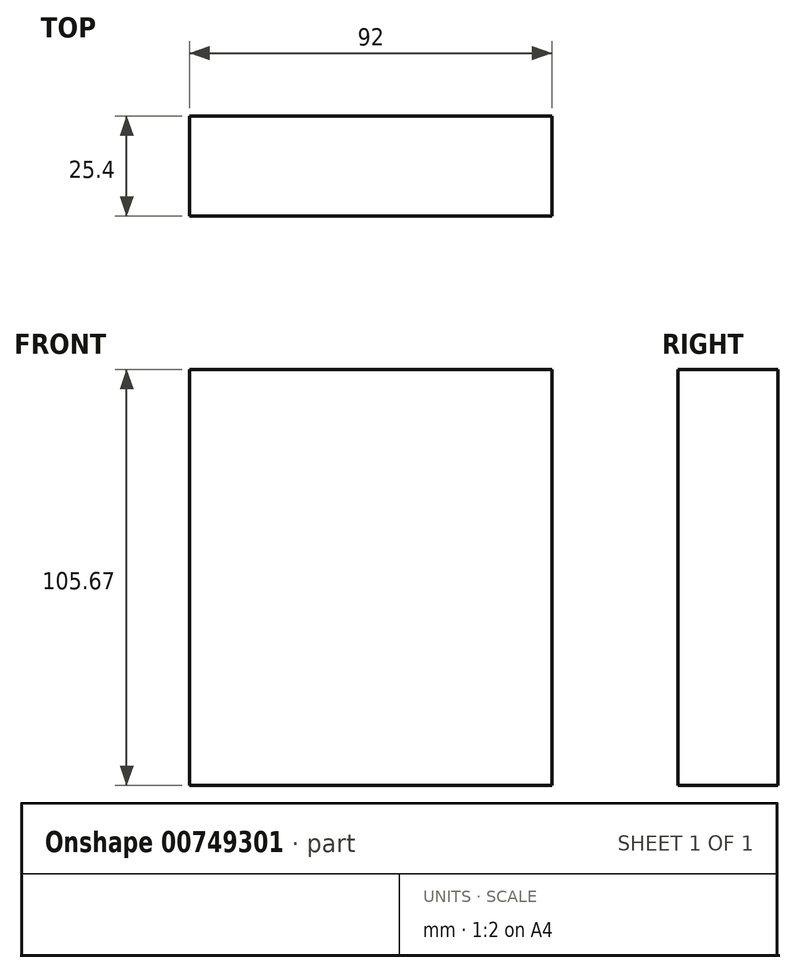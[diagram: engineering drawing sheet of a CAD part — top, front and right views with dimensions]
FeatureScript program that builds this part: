
annotation { "Feature Type Name" : "Feature", "Feature Type Description" : "" }
export const myFeature = defineFeature(function(context is Context, id is Id, definition is map)
    precondition{}
    {
        {
            var Q0;
            Q0=qCreatedBy(makeId("Front.planeOp"),FACE);
            var sketch = newSketch(context, id + "F0", { "sketchPlane" : qUnion([Q0])});
            skLineSegment(sketch, "E0.bottom", {"start": v(-216.81, 10.78) * mm, "end": v(-124.81, 10.78) * mm});
            skLineSegment(sketch, "E0.top", {"start": v(-216.81, -94.9) * mm, "end": v(-124.81, -94.9) * mm});
            skLineSegment(sketch, "E0.left", {"start": v(-216.81, 10.78) * mm, "end": v(-216.81, -94.9) * mm});
            skLineSegment(sketch, "E0.right", {"start": v(-124.81, 10.78) * mm, "end": v(-124.81, -94.9) * mm});
            skSolve(sketch);
        }
        {
            var Q0;
            Q0 = qSketchRegion(id + "F0", true);
            extrude(context, id + "F1", {"entities" : qUnion([Q0]), "depth" : 25.4 * mm, "offsetDistance" : 25.4 * mm});
        }
    });
